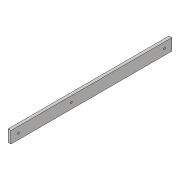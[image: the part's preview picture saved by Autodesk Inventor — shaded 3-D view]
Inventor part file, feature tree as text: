
AUTODESK INVENTOR PART (.ipt)
format: ipt  version: 2018.3 (Build 223284000, 284)  size: 95,232 bytes
history: native  units: in
note: dims shown in document units (in); Inventor stores cm internally (conversion verified against a paired STEP export)
features: hole x3, extrude x2, sketch x2
ambient origin geometry x8: Origin, YZ Plane, XZ Plane, XY Plane, X Axis, Y Axis, Z Axis, Center Point
bodies: Solid1 (feature_tree)
feature tree (7):
  extrude  "Extrusion1"  Depth=0.125in
  extrude  "Extrusion2"  Depth=6.895in
  hole  "Hole1"  [1 undecoded]
  hole  "Hole2"  [1 undecoded]
  hole  "Hole3"  [1 undecoded]
  sketch  "Sketch1"  dims[d0=0.5in d1=0.125in]
  sketch  "Sketch2"  dims[d2=6.895in d3=0.0in d4=0.0625in d5=0.3125in d6=1.0in d7=0.0in d8=4.0in d9=2.27in d10=0.0625in d11=0.0625in d12=1.0in d13=1.0in d14=0.085in d15=0.224in d16=0.375in d17=0.25in d18=0.5635in d19=0.349in d20=0.8108in d21=1.0in d22=1.0in d23=0.085in d24=0.224in d25=0.375in d26=0.25in d27=0.5635in d28=0.349in d29=0.8108in d30=1.0in d31=1.0in d32=0.085in d33=0.224in d34=0.375in d35=0.25in d36=0.5635in d37=0.349in d38=0.8108in]
note: 3 required parameter values undecoded (feature->parameter linkage not recoverable at this tier; creation-order binding heuristic only, values carry confidence <= 0.55)
